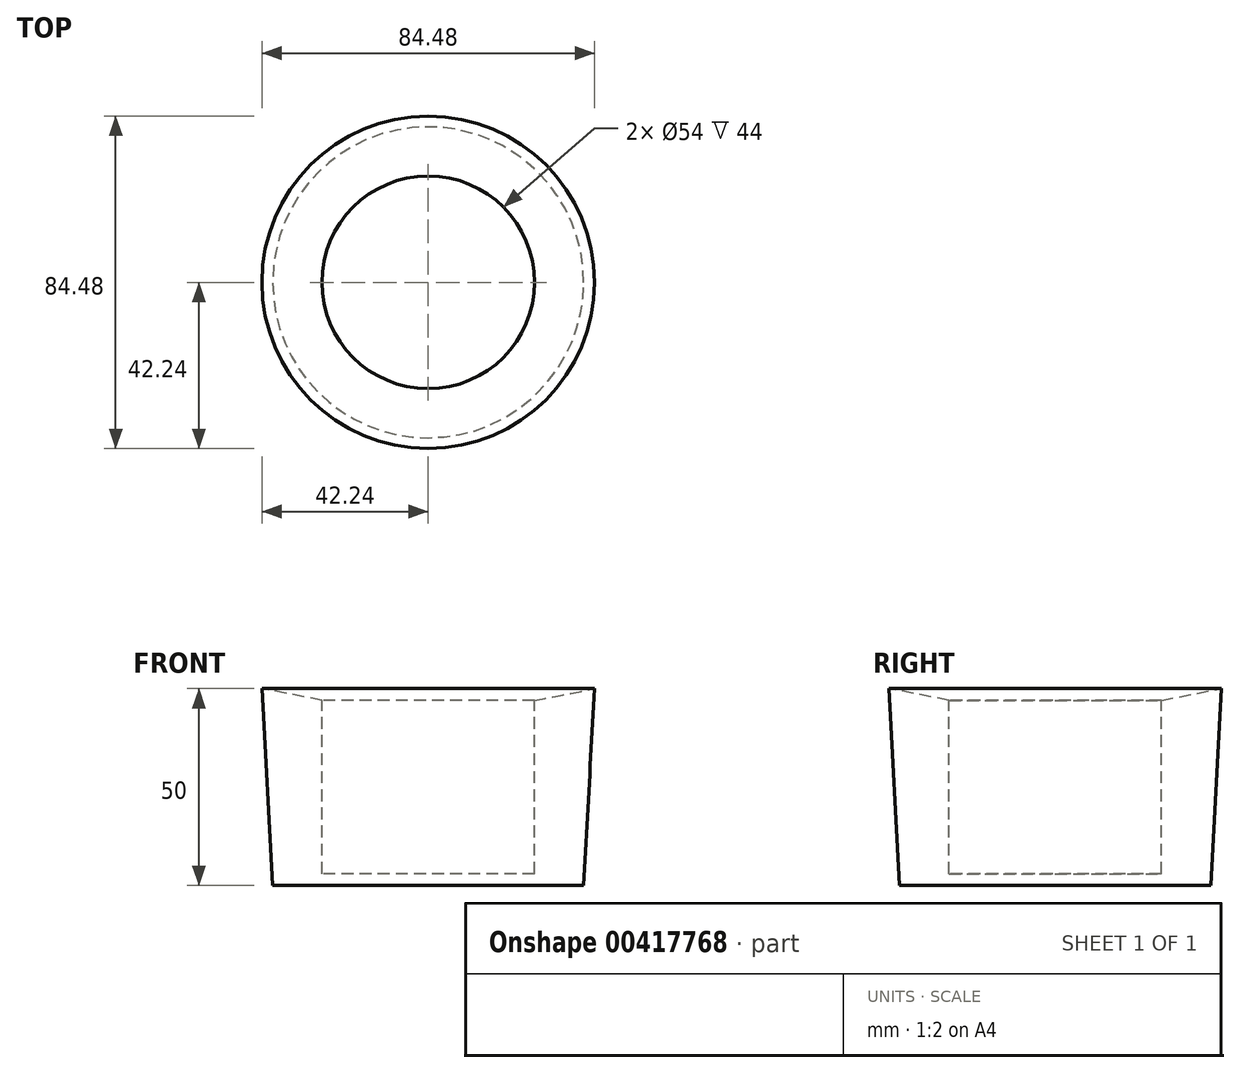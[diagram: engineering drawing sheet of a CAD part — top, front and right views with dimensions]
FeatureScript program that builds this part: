
annotation { "Feature Type Name" : "Feature", "Feature Type Description" : "" }
export const myFeature = defineFeature(function(context is Context, id is Id, definition is map)
    precondition{}
    {
        {
            var Q0;
            Q0=qCreatedBy(makeId("Front.planeOp"),FACE);
            var sketch = newSketch(context, id + "F0", { "sketchPlane" : qUnion([Q0])});
            skLineSegment(sketch, "E0", {"start": v(0, 0) * mm, "end": v(-39.5, 0) * mm});
            skLineSegment(sketch, "E1", {"start": v(-39.5, 0) * mm, "end": v(-42.24, 50) * mm});
            skLineSegment(sketch, "E2", {"start": v(-42.24, 50) * mm, "end": v(-27, 47) * mm});
            skLineSegment(sketch, "E3", {"start": v(-27, 47) * mm, "end": v(-27, 3) * mm});
            skLineSegment(sketch, "E4", {"start": v(-27, 3) * mm, "end": v(0, 3) * mm});
            skLineSegment(sketch, "E5", {"start": v(0, 3) * mm, "end": v(0, 0) * mm});
            skSolve(sketch);
        }
        {
            var Q0;
            Q0=makeQuery(id+"F0.imprint","IMPRINT",FACE,{"disambiguationData":[TD([[makeQuery(id+"F0.imprint","IMPRINT",EDGE,{"derivedFrom":sQuery(id+"F0.wireOp",EDGE,"E0")}),-1.0]])]});
            var Q1;
            Q1=sQuery(id+"F0.wireOp",EDGE,"E5");
            revolve(context, id + "F1", {"entities" : qUnion([Q0]), "axis" : qUnion([Q1]), "revolveType" : RevolveType.FULL});
        }
    });
